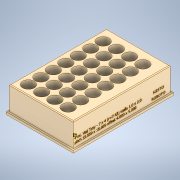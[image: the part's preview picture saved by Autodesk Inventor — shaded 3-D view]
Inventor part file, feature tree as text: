
AUTODESK INVENTOR PART (.ipt)
format: ipt  version: 2020 (Build 240168000, 168)  size: 2,262,016 bytes
history: native  units: in
note: dims shown in document units (in); Inventor stores cm internally (conversion verified against a paired STEP export)
features: sketch x4, extrude x2, hole x1, pattern_linear x1, fillet x1, emboss x1
ambient origin geometry x8: Origin, YZ Plane, XZ Plane, XY Plane, X Axis, Y Axis, Z Axis, Center Point
bodies: Solid1 (feature_tree)
feature tree (10):
  extrude  "Extrusion1"  TaperAngle=45.0deg  [1 undecoded]
  extrude  "Extrusion2"  TaperAngle=225.0deg  [1 undecoded]
  hole  "Hole2"  [1 undecoded]
  pattern_linear  "Rectangular Pattern1"  Spacing1=0.585in  [1 undecoded]
  fillet  "Fillet1"  Radius=0.75in
  emboss  "Emboss2"
  sketch  "Sketch1"  dims[d3=0.0in d5=45.0deg]
  sketch  "Sketch2"  dims[d6=0.1181in d7=225.0deg]
  sketch  "Sketch4"  dims[d9=0.0in d30=0.673in]
  sketch  "Sketch5"  dims[d31=45.0deg d32=0.585in d33=0.75in d34=0.375in d35=0.25in d36=0.5635in d38=0.0in d41=0.6244in d44=0.6637in d48=0.0394in d49=0.0in]
note: 4 required parameter values undecoded (feature->parameter linkage not recoverable at this tier; creation-order binding heuristic only, values carry confidence <= 0.55)
